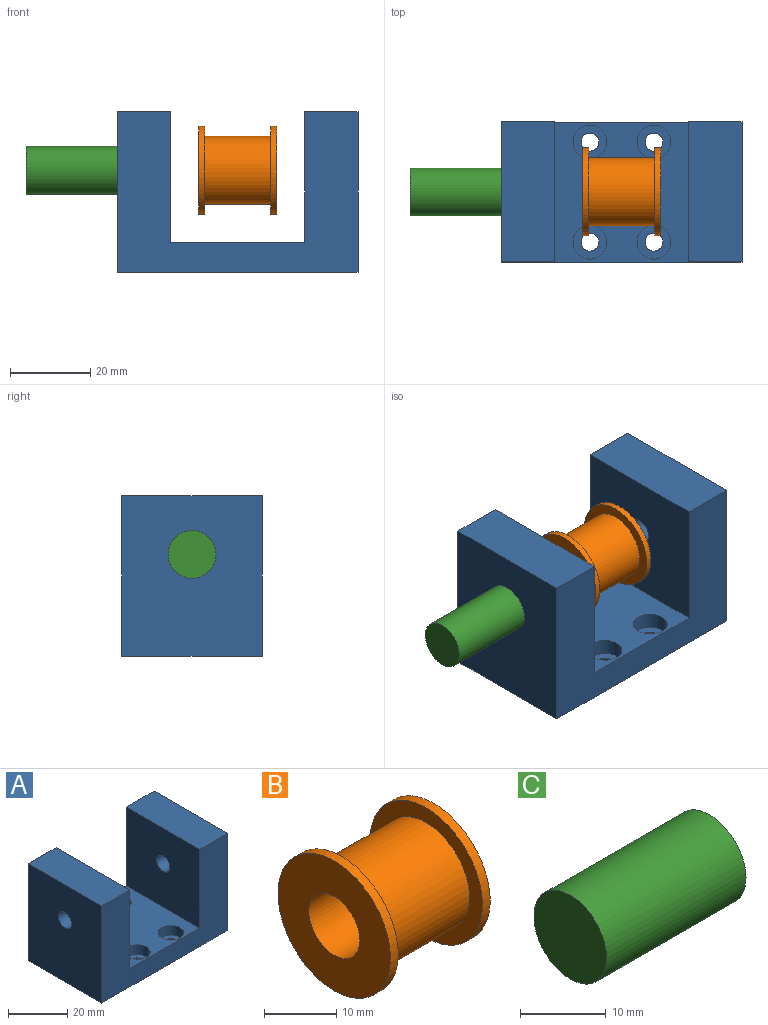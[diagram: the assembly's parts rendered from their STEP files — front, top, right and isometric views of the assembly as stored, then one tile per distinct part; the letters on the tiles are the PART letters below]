
ASSEMBLY  parts=3 mates=2
PART A: 24 faces, bbox 60x35x40 mm
  f0: plane 40x35mm, normal (1,0,0), area 1368.3mm2, adj f1,f7,f8,f9,f23
  f1: plane 35x13.25mm, normal (0,0,1), area 463.7mm2, adj f0,f2,f8,f9
  f2: plane 35x32.5mm, normal (-1,0,0), area 1105.8mm2, adj f1,f3,f8,f9,f23
  f3: plane 35x33.5mm, normal (0,0,1), area 945.5mm2, adj f2,f4,f8,f9,f10,f12,f14,f16
  f4: plane 35x32.5mm, normal (1,0,0), area 1105.8mm2, adj f3,f5,f8,f9,f22
  f5: plane 35x13.25mm, normal (0,0,1), area 463.7mm2, adj f4,f6,f8,f9
  f6: plane 40x35mm, normal (-1,0,0), area 1368.3mm2, adj f5,f7,f8,f9,f22
  f7: plane 60x35mm, normal (0,0,-1), area 2036.4mm2, adj f0,f6,f8,f9,f18,f19,f20,f21
  f8: plane 60x40mm, normal (0,-1,0), area 1311.2mm2, adj f0,f1,f2,f3,f4,f5,f6,f7
  f9: plane 60x40mm, normal (0,1,0), area 1311.2mm2, adj f0,f1,f2,f3,f4,f5,f6,f7
  f10: cylinder r=4.25mm len=8.5mm, axis (0,0,1), area 106.8mm2, adj f3,f11
  f11: plane 8.5x8.5mm, normal (0,0,1), area 40.8mm2, adj f10,f21
  f12: cylinder r=4.25mm len=8.5mm, axis (0,0,1), area 106.8mm2, adj f3,f13
  f13: plane 8.5x8.5mm, normal (0,0,1), area 40.8mm2, adj f12,f18
  f14: cylinder r=4.25mm len=8.5mm, axis (0,0,1), area 106.8mm2, adj f3,f15
  f15: plane 8.5x8.5mm, normal (0,0,1), area 40.8mm2, adj f14,f19
  f16: cylinder r=4.25mm len=8.5mm, axis (0,0,1), area 106.8mm2, adj f3,f17
  f17: plane 8.5x8.5mm, normal (0,0,1), area 40.8mm2, adj f16,f20
  f18: cylinder r=2.25mm len=4.5mm, axis (0,0,1), area 49.5mm2, adj f7,f13
  f19: cylinder r=2.25mm len=4.5mm, axis (0,0,1), area 49.5mm2, adj f7,f15
  f20: cylinder r=2.25mm len=4.5mm, axis (0,0,1), area 49.5mm2, adj f7,f17
  f21: cylinder r=2.25mm len=4.5mm, axis (0,0,1), area 49.5mm2, adj f7,f11
  f22: cylinder r=3.17mm len=13.25mm, axis (1,0,0), area 264.3mm2, adj f4,f6
  f23: cylinder r=3.17mm len=13.25mm, axis (1,0,0), area 264.3mm2, adj f0,f2
PART B: 8 faces, bbox 19.5x22x22 mm
  f0: cylinder r=11mm len=22mm, axis (-1,0,0), area 103.7mm2, adj f4,f6
  f1: cylinder r=5mm len=19.5mm, axis (-1,0,0), area 612.6mm2, adj f3,f4
  f2: cylinder r=11mm len=22mm, axis (-1,0,0), area 103.7mm2, adj f3,f7
  f3: plane 22x22mm, normal (1,0,0), area 301.6mm2, adj f1,f2
  f4: plane 22x22mm, normal (-1,0,0), area 301.6mm2, adj f0,f1
  f5: cylinder r=8.5mm len=17mm, axis (1,0,0), area 881.2mm2, adj f6,f7
  f6: plane 22x22mm, normal (1,0,0), area 153.2mm2, adj f0,f5
  f7: plane 22x22mm, normal (-1,0,0), area 153.2mm2, adj f2,f5
PART C: 3 faces, bbox 23x12x12 mm
  f0: cylinder r=6mm len=23mm, axis (1,0,0), area 867.1mm2, adj f1,f2
  f1: plane 12x12mm, normal (-1,0,0), area 113.1mm2, adj f0
  f2: plane 12x12mm, normal (1,0,0), area 113.1mm2, adj f0
PLACE A at identity fixed
PLACE B at identity
PLACE C at identity
MATE fastened C.f0 <-> A.f22  axis (1,0,0) through (-30,0,25.4)mm
MATE fastened B.f0 <-> A.f22  axis (1,0,0) through (0,0,25.4)mm
